# Revit family: DC_Holyoake_OutsideLouver_OHL-F-34_supply_12
name_source: partatom
category: Air Terminals
revit_build: Autodesk Revit 2013 (Build: 20120221_2030(x64)
units: mm (PartAtom-declared; Revit-internal decimal feet)

## types (1)
- OHL-F-34
    Accessories = Aluminium Bird mesh or insect mesh (fibreglass)
    Blade Array Count = 13.615789
    Blade Count = 13
    Blade Cut Setout = 494 mm  [stored 1.62073 ft]
    Blade Height = 56.77 mm  [stored 0.186253 ft]
    Blade Length = 397.4 mm  [stored 1.30381 ft]
    Blade Offset = 2.08 mm
    Blade Pitch = 38 mm  [stored 0.124672 ft]
    Description = Weather Louvres shall be Holyoake Model OHL-F-34 curved profile 34mm louvred blades set at 38mm centres and constructed in a 25mm flanged (F) frame to suit the installation profile.  Weather Louvres shall be of extruded aluminium construction and finished in natural anodised or powdercoat and fitted with accessories and dampers where indicated as manufactured by Holyoake.
    Exact Neck Height = 520 mm  [stored 1.70604 ft]
    Exact Neck Width = 400 mm  [stored 1.31234 ft]
    Exact Overall Flange Height = 568.2 mm  [stored 1.86417 ft]
    Exact Overall Flange Width = 448.2 mm
    Flange Thickness = 4.7 mm
    Flange Width = 25.4 mm  [stored 0.0833333 ft]
    Holyoake Product Range = Outside Louvres
    Louver Depth = 38.3 mm  [stored 0.125656 ft]
    Manufacturer = Holyoake
    Material - Body = Holyoake Aluminium
    Material - Face = Holyoake Aluminium
    Max Flow = 2000.0 L/s
    Min Flow = 100.0 L/s
    Model = OHL-F-34
    Noise Level NC Max = 0.00 NC
    Noise Level NC Min = 0.00 NC
    Nominal Height = 526 mm  [stored 1.72572 ft]
    Nominal Width = 406 mm  [stored 1.33202 ft]
    Overall Opening = 517.4 mm  [stored 1.69751 ft]
    Static Pressure Min = 0.0 Pa
    Top Blade Height = 23.4 mm
    Type Comments = 34mm Horizontal Curved Profile Louvers in Flanged Surround
    URL = http://www.holyoake.com

note: [stored X ft] marks values corroborated as IEEE doubles in the binary element streams (Revit-internal decimal feet)

## geometry (parser evidence)
native form markers: Blend x6, Sweep x7
no freeform markers — native parametric forms only
